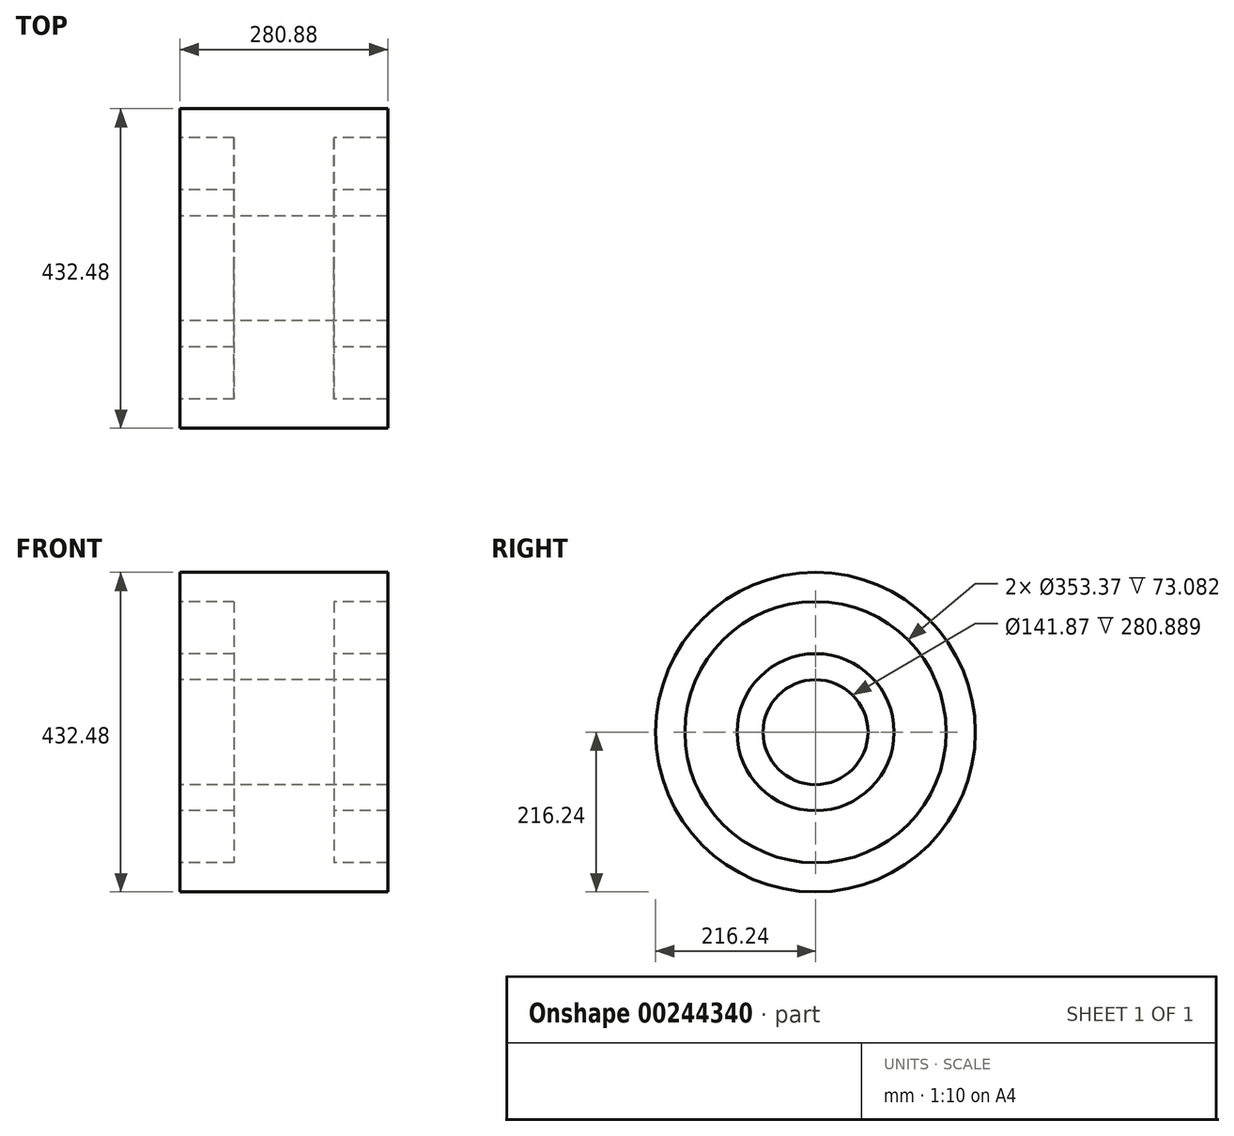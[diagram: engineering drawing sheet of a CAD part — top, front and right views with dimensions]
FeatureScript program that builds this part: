
annotation { "Feature Type Name" : "Feature", "Feature Type Description" : "" }
export const myFeature = defineFeature(function(context is Context, id is Id, definition is map)
    precondition{}
    {
        {
            var Q0;
            Q0=qCreatedBy(makeId("Front.planeOp"),FACE);
            var sketch = newSketch(context, id + "F0", { "sketchPlane" : qUnion([Q0])});
            skLineSegment(sketch, "E0", {"start": v(-98.33, 0) * mm, "end": v(146.83, 0) * mm, "construction": true});
            skLineSegment(sketch, "E1", {"start": v(0, 0) * mm, "end": v(0, 238.6) * mm, "construction": true});
            skLineSegment(sketch, "E2", {"start": v(0, 216.24) * mm, "end": v(140.44, 216.24) * mm});
            skLineSegment(sketch, "E3", {"start": v(140.44, 216.24) * mm, "end": v(140.44, 176.69) * mm});
            skLineSegment(sketch, "E4", {"start": v(140.44, 176.69) * mm, "end": v(67.36, 176.69) * mm});
            skLineSegment(sketch, "E5", {"start": v(67.36, 176.69) * mm, "end": v(67.36, 106.18) * mm});
            skLineSegment(sketch, "E6", {"start": v(67.36, 106.18) * mm, "end": v(140.44, 106.18) * mm});
            skLineSegment(sketch, "E7", {"start": v(140.44, 106.18) * mm, "end": v(140.44, 70.93) * mm});
            skLineSegment(sketch, "E8", {"start": v(140.44, 70.93) * mm, "end": v(0, 70.93) * mm});
            skLineSegment(sketch, "E9.MirrorCS", {"start": v(0, 216.24) * mm, "end": v(-140.44, 216.24) * mm});
            skLineSegment(sketch, "E10.MirrorCS", {"start": v(-140.44, 216.24) * mm, "end": v(-140.44, 176.69) * mm});
            skLineSegment(sketch, "E11.MirrorCS", {"start": v(-140.44, 176.69) * mm, "end": v(-67.36, 176.69) * mm});
            skLineSegment(sketch, "E12.MirrorCS", {"start": v(-67.36, 176.69) * mm, "end": v(-67.36, 106.18) * mm});
            skLineSegment(sketch, "E13.MirrorCS", {"start": v(-67.36, 106.18) * mm, "end": v(-140.44, 106.18) * mm});
            skLineSegment(sketch, "E14.MirrorCS", {"start": v(-140.44, 106.18) * mm, "end": v(-140.44, 70.93) * mm});
            skLineSegment(sketch, "E15.MirrorCS", {"start": v(-140.44, 70.93) * mm, "end": v(0, 70.93) * mm});
            skSolve(sketch);
        }
        {
            var Q0;
            Q0 = qSketchRegion(id + "F0", true);
            var Q1;
            Q1=sQuery(id+"F0.wireOp",EDGE,"E0");
            revolve(context, id + "F1", {"entities" : qUnion([Q0]), "axis" : qUnion([Q1]), "revolveType" : RevolveType.FULL});
        }
    });
